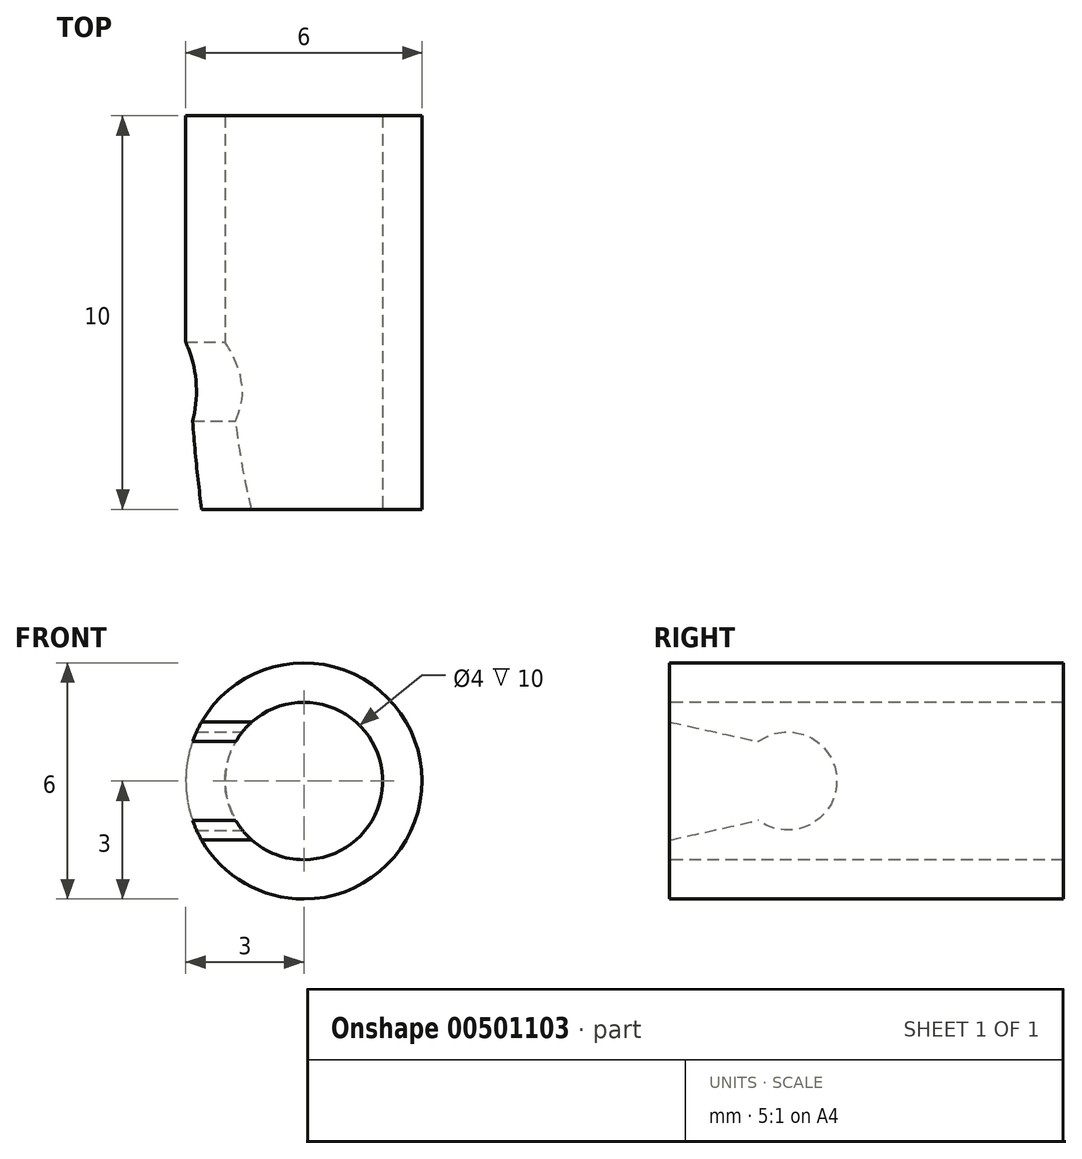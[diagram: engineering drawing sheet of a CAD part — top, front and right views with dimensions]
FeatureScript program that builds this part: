
annotation { "Feature Type Name" : "Feature", "Feature Type Description" : "" }
export const myFeature = defineFeature(function(context is Context, id is Id, definition is map)
    precondition{}
    {
        {
            var Q0;
            Q0=qCreatedBy(makeId("Front.planeOp"),FACE);
            var sketch = newSketch(context, id + "F0", { "sketchPlane" : qUnion([Q0])});
            skCircle(sketch, "E0", {"center": v(0, 0) * mm, "radius": 3 * mm});
            skSolve(sketch);
        }
        {
            var Q0;
            Q0 = qSketchRegion(id + "F0", true);
            extrude(context, id + "F1", {"entities" : qUnion([Q0]), "oppositeDirection" : true, "depth" : 10 * mm});
        }
        {
            var Q0;
            Q0=qCreatedBy(makeId("Right.planeOp"),FACE);
            var sketch = newSketch(context, id + "F2", { "sketchPlane" : qUnion([Q0])});
            skLineSegment(sketch, "E1", {"start": v(0, 0) * mm, "end": v(0, -1.5) * mm});
            skLineSegment(sketch, "E2", {"start": v(0, 0) * mm, "end": v(0, 1.5) * mm});
            skArc(sketch, "E3", {"start": v(2.25, -1) * mm, "mid": v(4.25, 0) * mm, "end": v(2.25, 1) * mm});
            skLineSegment(sketch, "E4", {"start": v(0, -1.5) * mm, "end": v(2.25, -1) * mm});
            skLineSegment(sketch, "E5", {"start": v(0, 1.5) * mm, "end": v(2.25, 1) * mm});
            skSolve(sketch);
        }
        {
            var Q0;
            Q0 = qSketchRegion(id + "F2", true);
            extrude(context, id + "F3", {"entities" : qUnion([Q0]), "operationType" : NewBodyOperationType.REMOVE, "oppositeDirection" : true, "depth" : 25 * mm});
        }
        {
            var Q0;
            Q0=qCreatedBy(makeId("Front.planeOp"),FACE);
            var sketch = newSketch(context, id + "F4", { "sketchPlane" : qUnion([Q0])});
            skCircle(sketch, "E6", {"center": v(0, 0) * mm, "radius": 2 * mm});
            skSolve(sketch);
        }
        {
            var Q0;
            Q0 = qSketchRegion(id + "F4", true);
            extrude(context, id + "F5", {"entities" : qUnion([Q0]), "operationType" : NewBodyOperationType.REMOVE, "oppositeDirection" : true, "depth" : 25 * mm});
        }
    });
